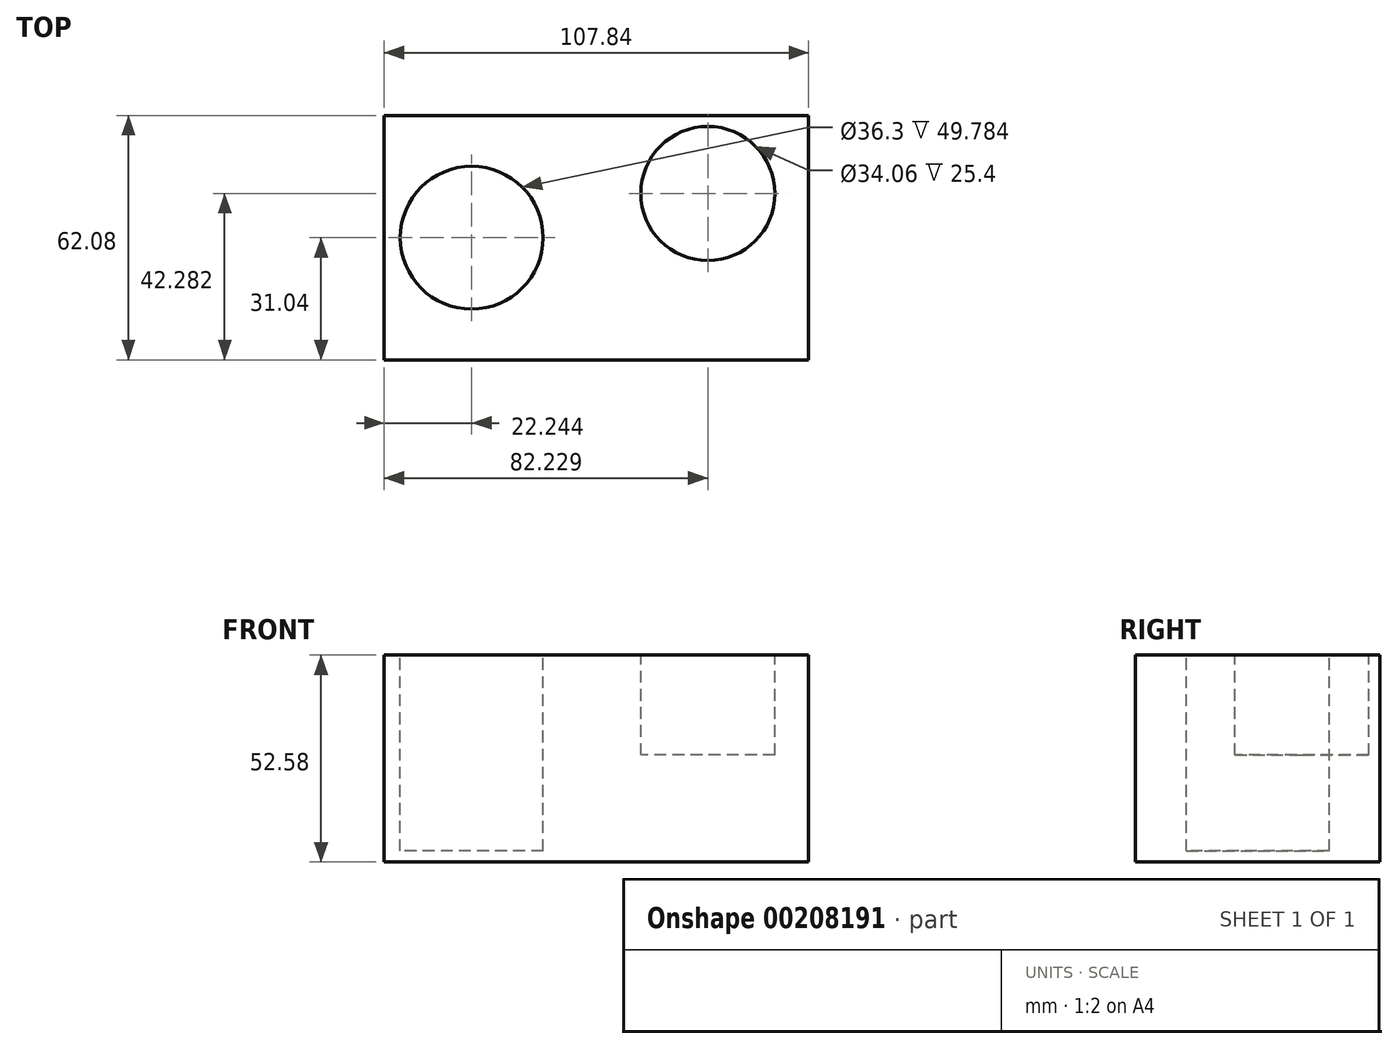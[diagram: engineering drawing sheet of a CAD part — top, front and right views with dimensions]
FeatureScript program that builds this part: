
annotation { "Feature Type Name" : "Feature", "Feature Type Description" : "" }
export const myFeature = defineFeature(function(context is Context, id is Id, definition is map)
    precondition{}
    {
        {
            var Q0;
            Q0=qCreatedBy(makeId("Top.planeOp"),FACE);
            var sketch = newSketch(context, id + "F0", { "sketchPlane" : qUnion([Q0])});
            skLineSegment(sketch, "E0.bottom", {"start": v(53.92, 31.04) * mm, "end": v(-53.92, 31.04) * mm});
            skLineSegment(sketch, "E0.top", {"start": v(53.92, -31.04) * mm, "end": v(-53.92, -31.04) * mm});
            skLineSegment(sketch, "E0.left", {"start": v(53.92, 31.04) * mm, "end": v(53.92, -31.04) * mm});
            skLineSegment(sketch, "E0.right", {"start": v(-53.92, 31.04) * mm, "end": v(-53.92, -31.04) * mm});
            skPoint(sketch, "E0.middle", {"position": v(0, 0) * mm});
            skSolve(sketch);
        }
        {
            var Q0;
            Q0=makeQuery(id+"F0.imprint","IMPRINT",FACE,{"disambiguationData":[TD([[makeQuery(id+"F0.imprint","IMPRINT",EDGE,{"derivedFrom":sQuery(id+"F0.wireOp",EDGE,"E0.bottom")}),1.0]])]});
            extrude(context, id + "F1", {"entities" : qUnion([Q0]), "depth" : 52.58 * mm});
        }
        {
            var Q0;
            Q0=makeQuery(id+"F1.opExtrude","CAP_FACE",FACE,{"disambiguationData":[OSD([sQuery(id+"F0.wireOp",EDGE,"E0.bottom"),sQuery(id+"F0.wireOp",EDGE,"E0.top"),sQuery(id+"F0.wireOp",EDGE,"E0.left"),sQuery(id+"F0.wireOp",EDGE,"E0.right")])],"isStart":false});
            var sketch = newSketch(context, id + "F2", { "sketchPlane" : qUnion([Q0])});
            skCircle(sketch, "E1", {"center": v(-31.68, 0) * mm, "radius": 18.15 * mm});
            skPoint(sketch, "E1.centerSnap0", {"position": v(-53.92, 0) * mm});
            skSolve(sketch);
        }
        {
            var Q0;
            Q0=makeQuery(id+"F2.imprint","IMPRINT",FACE,{"disambiguationData":[TD([[makeQuery(id+"F2.imprint","IMPRINT",EDGE,{"derivedFrom":sQuery(id+"F2.wireOp",EDGE,"E1")}),1.0]])]});
            extrude(context, id + "F3", {"entities" : qUnion([Q0]), "operationType" : NewBodyOperationType.REMOVE, "oppositeDirection" : true, "depth" : 49.78 * mm});
        }
        {
            var Q0;
            Q0=makeQuery(id+"F1.opExtrude","CAP_FACE",FACE,{"disambiguationData":[OSD([sQuery(id+"F0.wireOp",EDGE,"E0.bottom"),sQuery(id+"F0.wireOp",EDGE,"E0.top"),sQuery(id+"F0.wireOp",EDGE,"E0.left"),sQuery(id+"F0.wireOp",EDGE,"E0.right")])],"isStart":false});
            var sketch = newSketch(context, id + "F4", { "sketchPlane" : qUnion([Q0])});
            skCircle(sketch, "E2", {"center": v(28.3, 11.24) * mm, "radius": 17.03 * mm});
            skSolve(sketch);
        }
        {
            var Q0;
            Q0=makeQuery(id+"F4.imprint","IMPRINT",FACE,{"disambiguationData":[TD([[makeQuery(id+"F4.imprint","IMPRINT",EDGE,{"derivedFrom":sQuery(id+"F4.wireOp",EDGE,"E2")}),1.0]])]});
            extrude(context, id + "F5", {"entities" : qUnion([Q0]), "operationType" : NewBodyOperationType.REMOVE, "oppositeDirection" : true, "depth" : 25.4 * mm});
        }
    });
